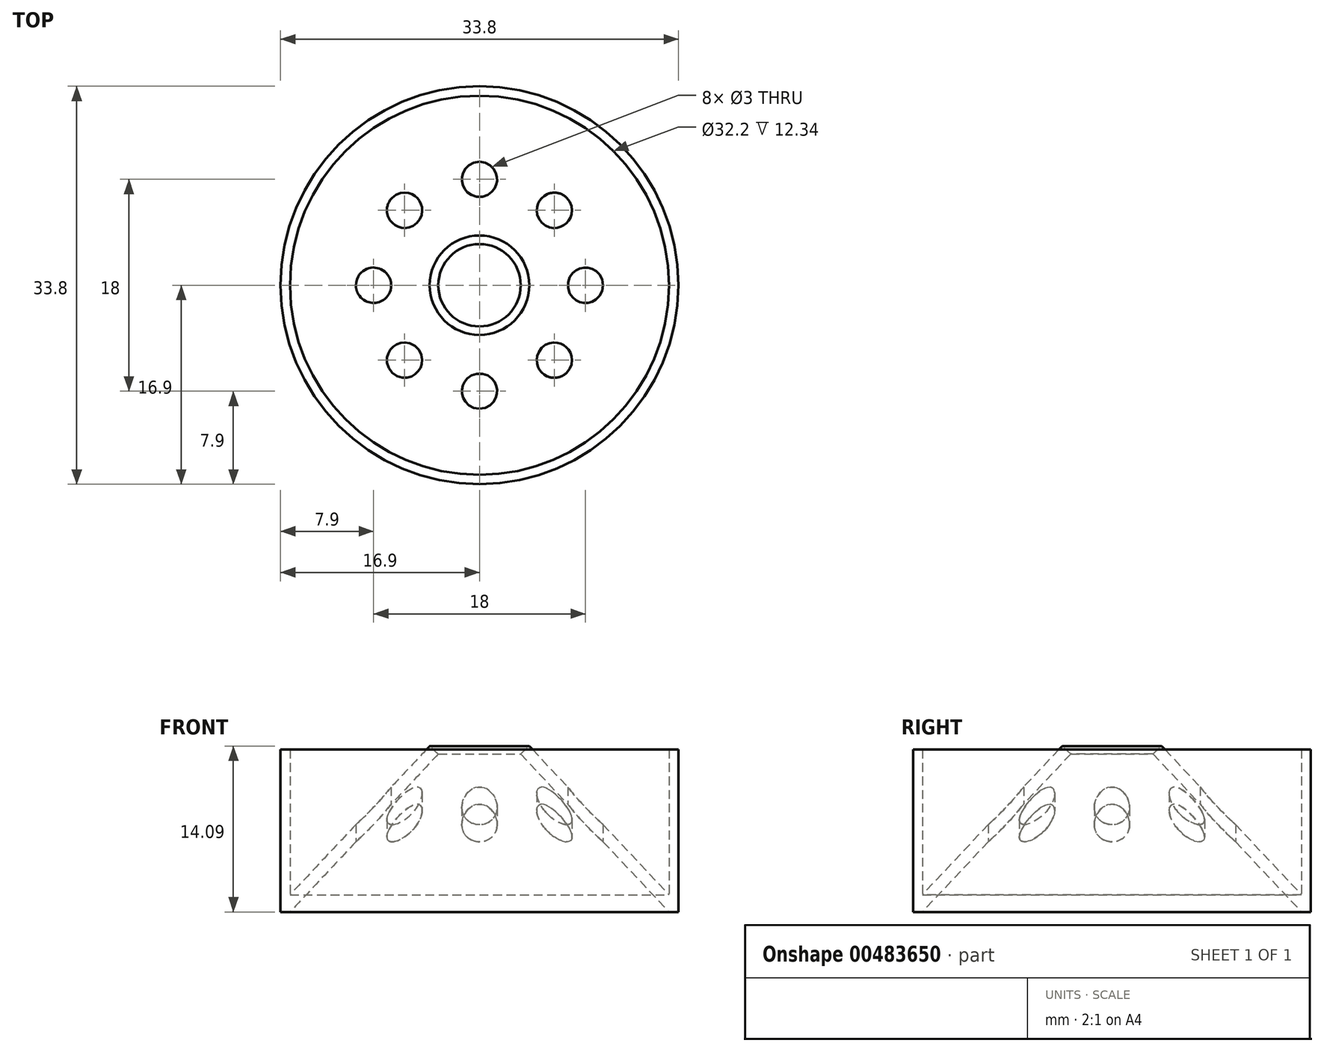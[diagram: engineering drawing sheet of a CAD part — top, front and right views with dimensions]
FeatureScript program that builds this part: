
annotation { "Feature Type Name" : "Feature", "Feature Type Description" : "" }
export const myFeature = defineFeature(function(context is Context, id is Id, definition is map)
    precondition{}
    {
        {
            var Q0;
            Q0=qCreatedBy(makeId("Front.planeOp"),FACE);
            var sketch = newSketch(context, id + "F0", { "sketchPlane" : qUnion([Q0])});
            skLineSegment(sketch, "E0", {"start": v(-16.9, 0) * mm, "end": v(-16.1, 0) * mm});
            skLineSegment(sketch, "E1", {"start": v(0, 0) * mm, "end": v(0, 14) * mm});
            skLineSegment(sketch, "E2", {"start": v(-3.5, 13.4) * mm, "end": v(-16.1, 0) * mm});
            skLineSegment(sketch, "E3", {"start": v(-16.9, 0) * mm, "end": v(-16.9, 13.8) * mm});
            skLineSegment(sketch, "E4", {"start": v(-16.9, 13.8) * mm, "end": v(-16.1, 13.8) * mm});
            skLineSegment(sketch, "E5", {"start": v(-3.5, 13.4) * mm, "end": v(-4.23, 14.1) * mm});
            skLineSegment(sketch, "E6", {"start": v(-4.23, 14.1) * mm, "end": v(-16.1, 1.46) * mm});
            skLineSegment(sketch, "E7", {"start": v(-16.1, 1.46) * mm, "end": v(-16.1, 13.8) * mm});
            skLineSegment(sketch, "E8", {"start": v(-3.5, 13.4) * mm, "end": v(0, 13.4) * mm});
            skLineSegment(sketch, "E9", {"start": v(0, 0) * mm, "end": v(-16.1, 0) * mm});
            skSolve(sketch);
        }
        {
            var Q0;
            Q0=makeQuery(id+"F0.imprint","IMPRINT",FACE,{"disambiguationData":[TD([[makeQuery(id+"F0.imprint","IMPRINT",EDGE,{"derivedFrom":sQuery(id+"F0.wireOp",EDGE,"E0")}),1.0]])]});
            var Q1;
            Q1=sQuery(id+"F0.wireOp",EDGE,"E1");
            revolve(context, id + "F1", {"entities" : qUnion([Q0]), "axis" : qUnion([Q1]), "revolveType" : RevolveType.FULL});
        }
        {
            var Q0;
            Q0=qCreatedBy(makeId("Top.planeOp"),FACE);
            var sketch = newSketch(context, id + "F2", { "sketchPlane" : qUnion([Q0])});
            skCircle(sketch, "E10", {"center": v(0, 9) * mm, "radius": 1.5 * mm});
            skCircle(sketch, "E11.1.0", {"center": v(-6.36, 6.36) * mm, "radius": 1.5 * mm});
            skCircle(sketch, "E11.2.0", {"center": v(-9, 0) * mm, "radius": 1.5 * mm});
            skCircle(sketch, "E11.3.0", {"center": v(-6.36, -6.36) * mm, "radius": 1.5 * mm});
            skCircle(sketch, "E11.4.0", {"center": v(0, -9) * mm, "radius": 1.5 * mm});
            skCircle(sketch, "E11.5.0", {"center": v(6.36, -6.36) * mm, "radius": 1.5 * mm});
            skCircle(sketch, "E11.6.0", {"center": v(9, 0) * mm, "radius": 1.5 * mm});
            skCircle(sketch, "E11.7.0", {"center": v(6.36, 6.36) * mm, "radius": 1.5 * mm});
            skPoint(sketch, "E11.center", {"position": v(0, 0) * mm});
            skSolve(sketch);
        }
        {
            var Q0;
            Q0=makeQuery(id+"F2.imprint","IMPRINT",FACE,{"disambiguationData":[TD([[makeQuery(id+"F2.imprint","IMPRINT",EDGE,{"derivedFrom":sQuery(id+"F2.wireOp",EDGE,"E11.3.0")}),1.0]])]});
            var Q1;
            Q1=makeQuery(id+"F2.imprint","IMPRINT",FACE,{"disambiguationData":[TD([[makeQuery(id+"F2.imprint","IMPRINT",EDGE,{"derivedFrom":sQuery(id+"F2.wireOp",EDGE,"E11.4.0")}),1.0]])]});
            var Q2;
            Q2=makeQuery(id+"F2.imprint","IMPRINT",FACE,{"disambiguationData":[TD([[makeQuery(id+"F2.imprint","IMPRINT",EDGE,{"derivedFrom":sQuery(id+"F2.wireOp",EDGE,"E11.5.0")}),1.0]])]});
            var Q3;
            Q3=makeQuery(id+"F2.imprint","IMPRINT",FACE,{"disambiguationData":[TD([[makeQuery(id+"F2.imprint","IMPRINT",EDGE,{"derivedFrom":sQuery(id+"F2.wireOp",EDGE,"E11.6.0")}),1.0]])]});
            var Q4;
            Q4=makeQuery(id+"F2.imprint","IMPRINT",FACE,{"disambiguationData":[TD([[makeQuery(id+"F2.imprint","IMPRINT",EDGE,{"derivedFrom":sQuery(id+"F2.wireOp",EDGE,"E11.7.0")}),1.0]])]});
            var Q5;
            Q5=makeQuery(id+"F2.imprint","IMPRINT",FACE,{"disambiguationData":[TD([[makeQuery(id+"F2.imprint","IMPRINT",EDGE,{"derivedFrom":sQuery(id+"F2.wireOp",EDGE,"E10")}),1.0]])]});
            var Q6;
            Q6=makeQuery(id+"F2.imprint","IMPRINT",FACE,{"disambiguationData":[TD([[makeQuery(id+"F2.imprint","IMPRINT",EDGE,{"derivedFrom":sQuery(id+"F2.wireOp",EDGE,"E11.1.0")}),1.0]])]});
            var Q7;
            Q7=makeQuery(id+"F2.imprint","IMPRINT",FACE,{"disambiguationData":[TD([[makeQuery(id+"F2.imprint","IMPRINT",EDGE,{"derivedFrom":sQuery(id+"F2.wireOp",EDGE,"E11.2.0")}),1.0]])]});
            extrude(context, id + "F3", {"entities" : qUnion([Q0, Q1, Q2, Q3, Q4, Q5, Q6, Q7]), "operationType" : NewBodyOperationType.REMOVE, "endBound" : BoundingType.THROUGH_ALL, "depth" : 25 * mm});
        }
    });
